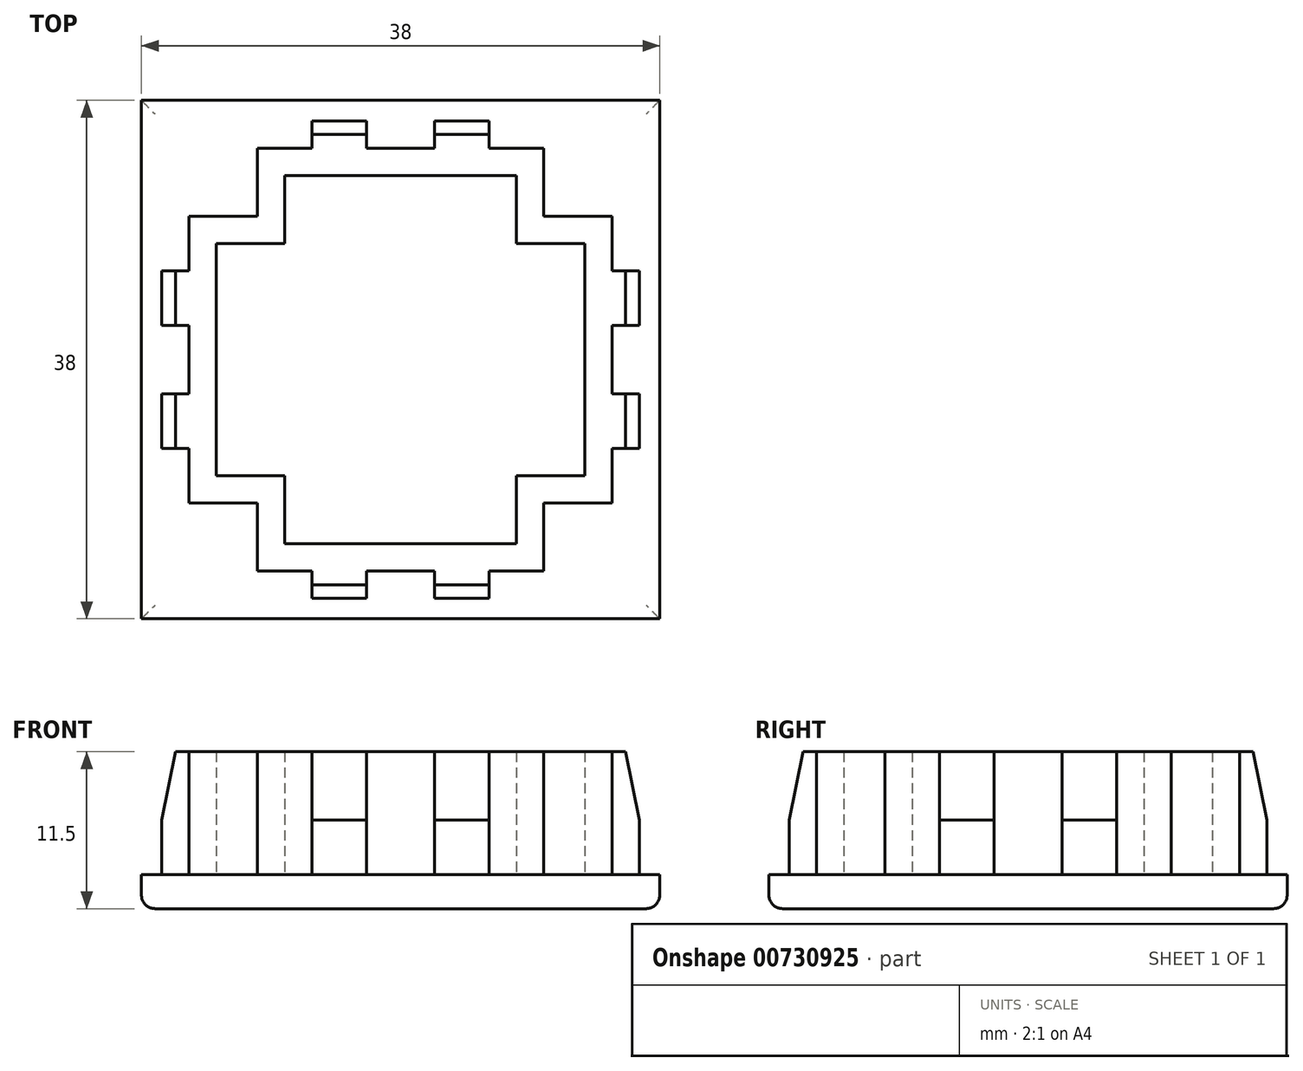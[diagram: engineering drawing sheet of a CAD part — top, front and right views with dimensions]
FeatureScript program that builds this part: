
annotation { "Feature Type Name" : "Feature", "Feature Type Description" : "" }
export const myFeature = defineFeature(function(context is Context, id is Id, definition is map)
    precondition{}
    {
        {
            var Q0;
            Q0=qCreatedBy(makeId("Top.planeOp"),FACE);
            var sketch = newSketch(context, id + "F0", { "sketchPlane" : qUnion([Q0])});
            skLineSegment(sketch, "E0.bottom", {"start": v(-19, 19) * mm, "end": v(19, 19) * mm});
            skLineSegment(sketch, "E0.top", {"start": v(-19, -19) * mm, "end": v(19, -19) * mm});
            skLineSegment(sketch, "E0.left", {"start": v(-19, 19) * mm, "end": v(-19, -19) * mm});
            skLineSegment(sketch, "E0.right", {"start": v(19, 19) * mm, "end": v(19, -19) * mm});
            skPoint(sketch, "E0.middle", {"position": v(0, 0) * mm});
            skSolve(sketch);
        }
        {
            var Q0;
            Q0 = qSketchRegion(id + "F0", true);
            extrude(context, id + "F1", {"entities" : qUnion([Q0]), "depth" : 2.5 * mm, "offsetDistance" : 25 * mm});
        }
        {
            var Q0;
            Q0=makeQuery(id+"F1.opExtrude","CAP_FACE",FACE,{"disambiguationData":[OSD([sQuery(id+"F0.wireOp",EDGE,"E0.bottom"),sQuery(id+"F0.wireOp",EDGE,"E0.top"),sQuery(id+"F0.wireOp",EDGE,"E0.left"),sQuery(id+"F0.wireOp",EDGE,"E0.right")])],"isStart":false});
            var sketch = newSketch(context, id + "F2", { "sketchPlane" : qUnion([Q0])});
            skLineSegment(sketch, "E1", {"start": v(-13.5, 0) * mm, "end": v(-13.5, 8.5) * mm});
            skPoint(sketch, "E1.startSnap0", {"position": v(-19, 0) * mm});
            skLineSegment(sketch, "E2", {"start": v(-13.5, 8.5) * mm, "end": v(-8.5, 8.5) * mm});
            skLineSegment(sketch, "E3.2", {"start": v(-15.5, 10.5) * mm, "end": v(-10.5, 10.5) * mm});
            skLineSegment(sketch, "E3.3", {"start": v(-15.5, 0) * mm, "end": v(-15.5, 2.5) * mm});
            skLineSegment(sketch, "E4", {"start": v(-15.5, 6.5) * mm, "end": v(-17.5, 6.5) * mm});
            skLineSegment(sketch, "E5", {"start": v(-17.5, 6.5) * mm, "end": v(-17.5, 2.5) * mm});
            skLineSegment(sketch, "E6", {"start": v(-17.5, 2.5) * mm, "end": v(-15.5, 2.5) * mm});
            skLineSegment(sketch, "E7.trimOffspring", {"start": v(-15.5, 6.5) * mm, "end": v(-15.5, 10.5) * mm});
            skLineSegment(sketch, "E8", {"start": v(-19, 19) * mm, "end": v(0, 0) * mm, "construction": true});
            skLineSegment(sketch, "E9.MirrorCS", {"start": v(-10.5, 15.5) * mm, "end": v(-10.5, 10.5) * mm});
            skLineSegment(sketch, "E10.MirrorCS", {"start": v(-6.5, 15.5) * mm, "end": v(-10.5, 15.5) * mm});
            skLineSegment(sketch, "E11.MirrorCS", {"start": v(-6.5, 15.5) * mm, "end": v(-6.5, 17.5) * mm});
            skLineSegment(sketch, "E12.MirrorCS", {"start": v(-6.5, 17.5) * mm, "end": v(-2.5, 17.5) * mm});
            skLineSegment(sketch, "E13.MirrorCS", {"start": v(-2.5, 17.5) * mm, "end": v(-2.5, 15.5) * mm});
            skLineSegment(sketch, "E14.MirrorCS", {"start": v(0, 15.5) * mm, "end": v(-2.5, 15.5) * mm});
            skLineSegment(sketch, "E15.MirrorCS", {"start": v(0, 13.5) * mm, "end": v(-8.5, 13.5) * mm});
            skLineSegment(sketch, "E16.MirrorCS", {"start": v(-8.5, 13.5) * mm, "end": v(-8.5, 8.5) * mm});
            skLineSegment(sketch, "E17", {"start": v(-15.5, 0) * mm, "end": v(-13.5, 0) * mm});
            skLineSegment(sketch, "E18", {"start": v(0, 15.5) * mm, "end": v(0, 13.5) * mm});
            skSolve(sketch);
        }
        {
            var Q0;
            Q0 = qSketchRegion(id + "F2", true);
            extrude(context, id + "F3", {"entities" : qUnion([Q0]), "depth" : 9 * mm, "offsetDistance" : 25 * mm});
        }
        {
            var Q0;
            Q0=makeQuery(id+"F3.opExtrude","CAP_EDGE",EDGE,{"disambiguationData":[OSD([sQuery(id+"F2.wireOp",EDGE,"E5")])],"isStart":false});
            var Q1;
            Q1=makeQuery(id+"F3.opExtrude","CAP_EDGE",EDGE,{"disambiguationData":[OSD([sQuery(id+"F2.wireOp",EDGE,"E12.MirrorCS")])],"isStart":false});
            chamfer(context, id + "F4", {"entities" : qUnion([Q0, Q1]), "chamferType" : ChamferType.TWO_OFFSETS, "width1" : 1 * mm, "oppositeDirection" : false, "width2" : 5 * mm, "tangentPropagation" : true});
        }
        {
            var Q0;
            Q0=qCreatedBy(makeId("Front.planeOp"),FACE);
            var sketch = newSketch(context, id + "F5", { "sketchPlane" : qUnion([Q0])});
            skLineSegment(sketch, "E19", {"start": v(0, 1.31) * mm, "end": v(0, 41.31) * mm, "construction": true});
            skSolve(sketch);
        }
        {
            var Q0;
            Q0=makeQuery(id+"F3.opExtrude","SWEPT_BODY",BODY,{"disambiguationData":[OSD([sQuery(id+"F2.wireOp",EDGE,"E1"),sQuery(id+"F2.wireOp",EDGE,"E2"),sQuery(id+"F2.wireOp",EDGE,"E3.2"),sQuery(id+"F2.wireOp",EDGE,"E3.3"),sQuery(id+"F2.wireOp",EDGE,"E4"),sQuery(id+"F2.wireOp",EDGE,"E5"),sQuery(id+"F2.wireOp",EDGE,"E6"),sQuery(id+"F2.wireOp",EDGE,"E7.trimOffspring"),sQuery(id+"F2.wireOp",EDGE,"E9.MirrorCS"),sQuery(id+"F2.wireOp",EDGE,"E10.MirrorCS"),sQuery(id+"F2.wireOp",EDGE,"E11.MirrorCS"),sQuery(id+"F2.wireOp",EDGE,"E12.MirrorCS"),sQuery(id+"F2.wireOp",EDGE,"E13.MirrorCS"),sQuery(id+"F2.wireOp",EDGE,"E14.MirrorCS"),sQuery(id+"F2.wireOp",EDGE,"E15.MirrorCS"),sQuery(id+"F2.wireOp",EDGE,"E16.MirrorCS"),sQuery(id+"F2.wireOp",EDGE,"E17"),sQuery(id+"F2.wireOp",EDGE,"E18")])]});
            var Q1;
            Q1=sQuery(id+"F5.wireOp",EDGE,"E19");
            circularPattern(context, id + "F6", {"operationType" : NewBodyOperationType.ADD, "entities" : qUnion([Q0]), "axis" : qUnion([Q1]), "angle" : 360 * degree, "instanceCount" : 4, "equalSpace" : true});
        }
        {
            var Q0;
            Q0=makeQuery(id+"F1.opExtrude","CAP_FACE",FACE,{"disambiguationData":[OSD([sQuery(id+"F0.wireOp",EDGE,"E0.bottom"),sQuery(id+"F0.wireOp",EDGE,"E0.top"),sQuery(id+"F0.wireOp",EDGE,"E0.left"),sQuery(id+"F0.wireOp",EDGE,"E0.right")])],"isStart":true});
            fillet(context, id + "F7", {"entities" : qUnion([Q0]), "radius" : 1 * mm, "tangentPropagation" : true, "allowEdgeOverflow" : false});
        }
    });
